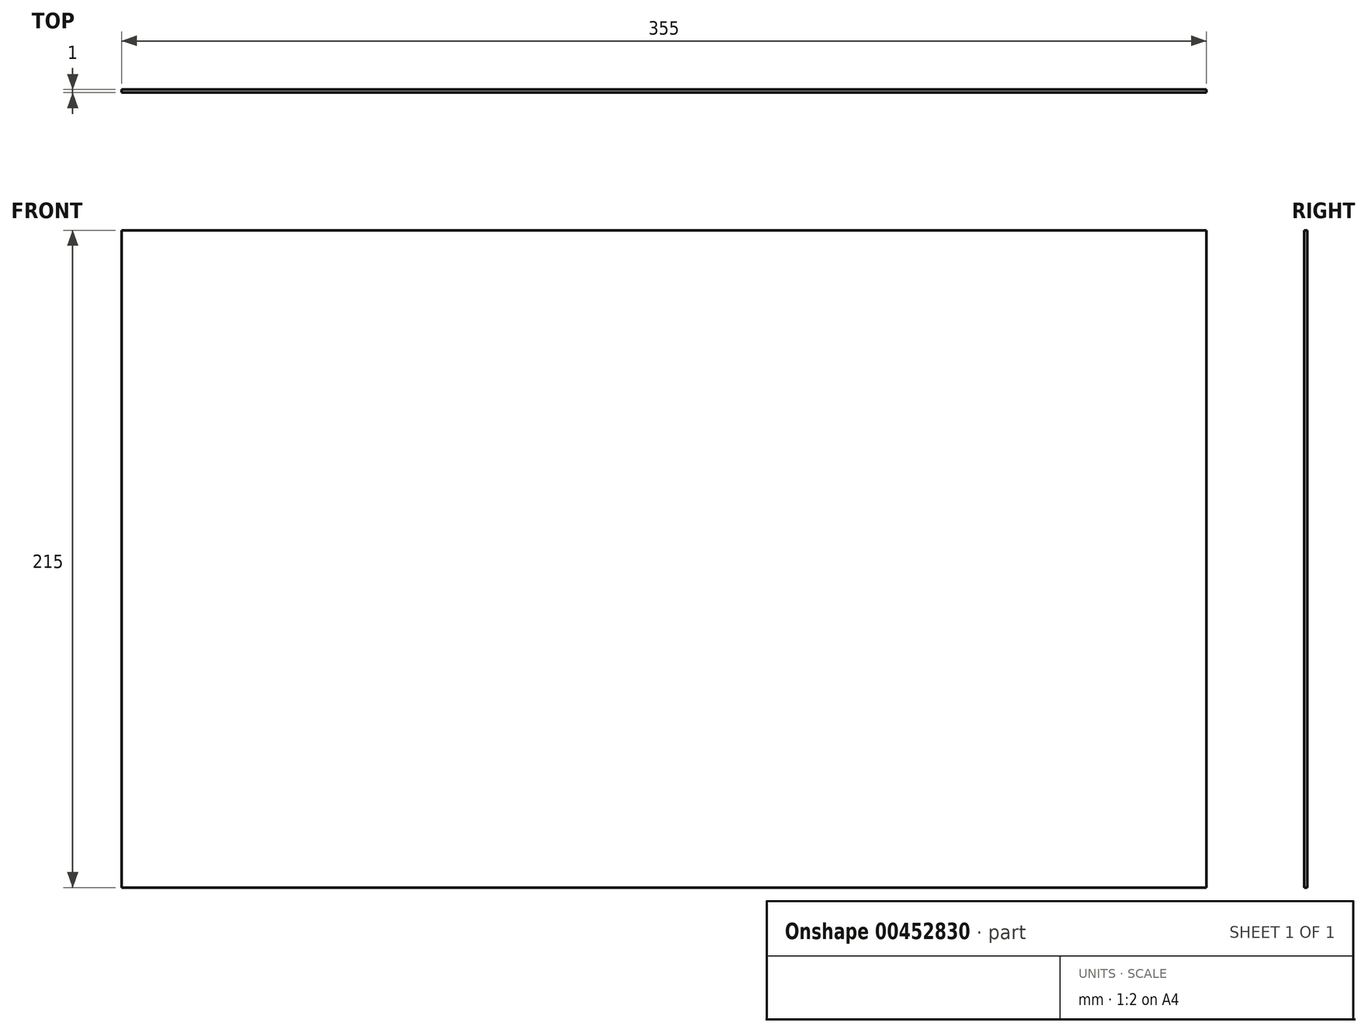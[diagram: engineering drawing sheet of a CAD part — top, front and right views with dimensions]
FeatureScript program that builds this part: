
annotation { "Feature Type Name" : "Feature", "Feature Type Description" : "" }
export const myFeature = defineFeature(function(context is Context, id is Id, definition is map)
    precondition{}
    {
        {
            var Q0;
            Q0=qCreatedBy(makeId("Front.planeOp"),FACE);
            var sketch = newSketch(context, id + "F0", { "sketchPlane" : qUnion([Q0])});
            skLineSegment(sketch, "E0.bottom", {"start": v(0, 0) * mm, "end": v(355, 0) * mm});
            skLineSegment(sketch, "E0.top", {"start": v(0, 215) * mm, "end": v(355, 215) * mm});
            skLineSegment(sketch, "E0.left", {"start": v(0, 0) * mm, "end": v(0, 215) * mm});
            skLineSegment(sketch, "E0.right", {"start": v(355, 0) * mm, "end": v(355, 215) * mm});
            skSolve(sketch);
        }
        {
            var Q0;
            Q0=makeQuery(id+"F0.imprint","IMPRINT",FACE,{"disambiguationData":[TD([[makeQuery(id+"F0.imprint","IMPRINT",EDGE,{"derivedFrom":sQuery(id+"F0.wireOp",EDGE,"E0.bottom")}),1.0]])]});
            extrude(context, id + "F1", {"entities" : qUnion([Q0]), "depth" : 1 * mm});
        }
    });
